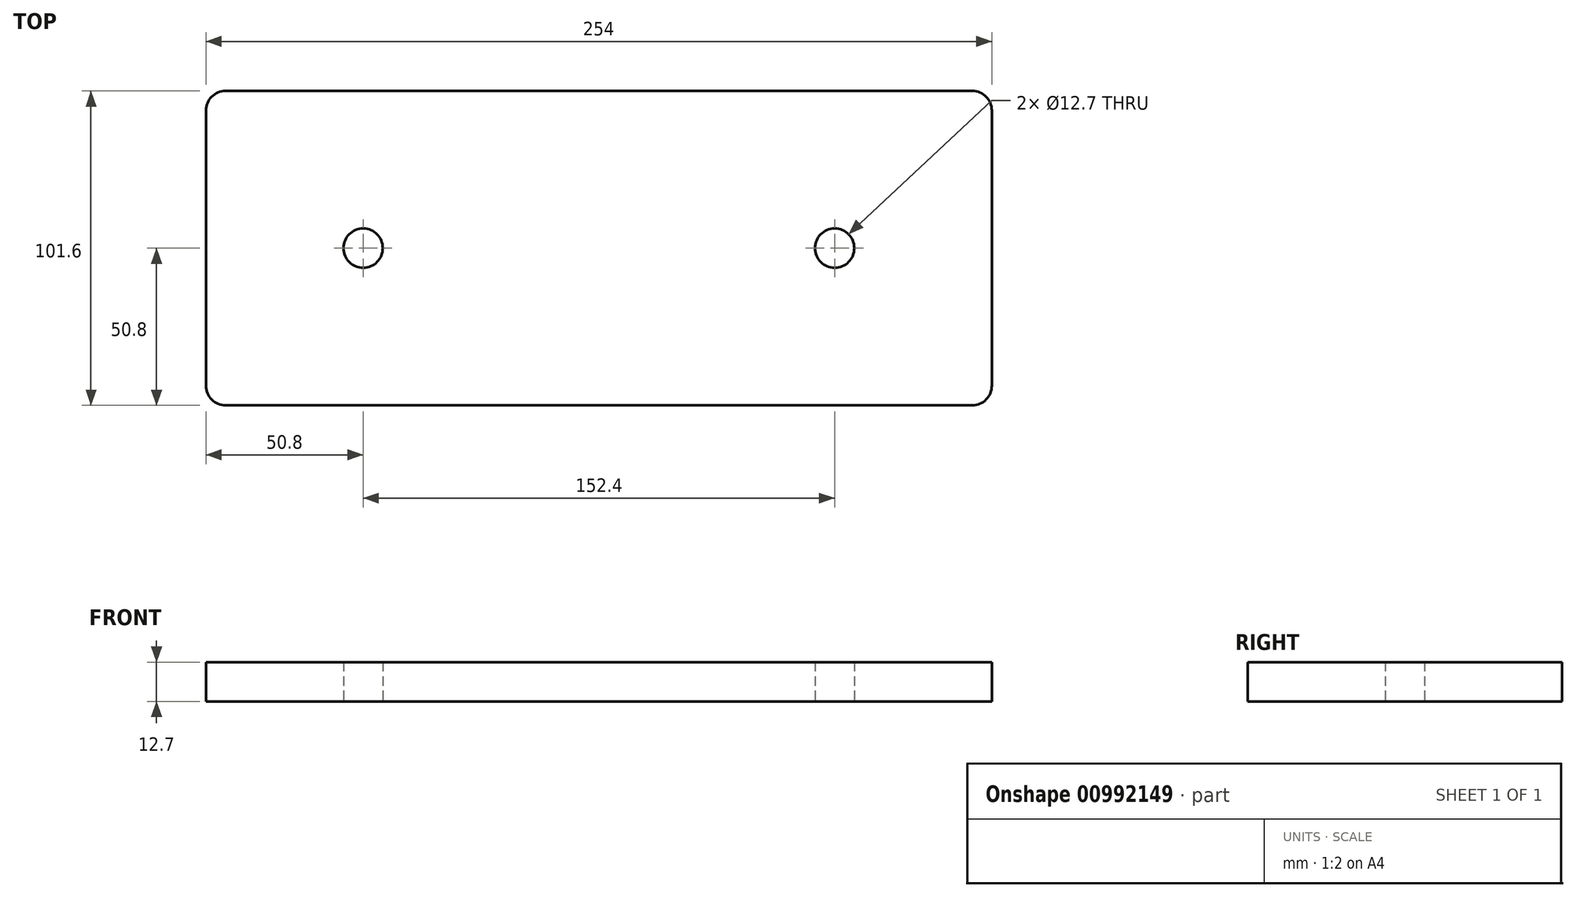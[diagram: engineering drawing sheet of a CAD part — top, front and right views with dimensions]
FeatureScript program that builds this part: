
annotation { "Feature Type Name" : "Feature", "Feature Type Description" : "" }
export const myFeature = defineFeature(function(context is Context, id is Id, definition is map)
    precondition{}
    {
        {
            var Q0;
            Q0=qCreatedBy(makeId("Top.planeOp"),FACE);
            var sketch = newSketch(context, id + "F0", { "sketchPlane" : qUnion([Q0])});
            skLineSegment(sketch, "E0.bottom", {"start": v(127, -50.8) * mm, "end": v(-127, -50.8) * mm});
            skLineSegment(sketch, "E0.top", {"start": v(127, 50.8) * mm, "end": v(-127, 50.8) * mm});
            skLineSegment(sketch, "E0.left", {"start": v(127, -50.8) * mm, "end": v(127, 50.8) * mm});
            skLineSegment(sketch, "E0.right", {"start": v(-127, -50.8) * mm, "end": v(-127, 50.8) * mm});
            skPoint(sketch, "E0.middle", {"position": v(0, 0) * mm});
            skPoint(sketch, "E1", {"position": v(-76.2, 0) * mm});
            skPoint(sketch, "E2", {"position": v(76.2, 0) * mm});
            skCircle(sketch, "E3", {"center": v(-76.2, 0) * mm, "radius": 6.35 * mm});
            skCircle(sketch, "E4", {"center": v(76.2, 0) * mm, "radius": 6.35 * mm});
            skPoint(sketch, "E5.orphan", {"position": v(-127, 0) * mm});
            skPoint(sketch, "E6.orphan", {"position": v(127, 0) * mm});
            skSolve(sketch);
        }
        {
            var Q0;
            Q0=makeQuery(id+"F0.imprint","IMPRINT",FACE,{"disambiguationData":[TD([[makeQuery(id+"F0.imprint","IMPRINT",EDGE,{"derivedFrom":sQuery(id+"F0.wireOp",EDGE,"E0.bottom")}),-1.0]])]});
            extrude(context, id + "F1", {"entities" : qUnion([Q0]), "depth" : 12.7 * mm, "offsetDistance" : 25.4 * mm});
        }
        {
            var Q0;
            Q0=makeQuery(id+"F1.opExtrude","SWEPT_EDGE",EDGE,{"disambiguationData":[OSD([sQuery(id+"F0.wireOp",EDGE,"E0.top"),sQuery(id+"F0.wireOp",EDGE,"E0.right")])]});
            var Q1;
            Q1=makeQuery(id+"F1.opExtrude","SWEPT_EDGE",EDGE,{"disambiguationData":[OSD([sQuery(id+"F0.wireOp",EDGE,"E0.bottom"),sQuery(id+"F0.wireOp",EDGE,"E0.right")])]});
            var Q2;
            Q2=makeQuery(id+"F1.opExtrude","SWEPT_EDGE",EDGE,{"disambiguationData":[OSD([sQuery(id+"F0.wireOp",EDGE,"E0.bottom"),sQuery(id+"F0.wireOp",EDGE,"E0.left")])]});
            var Q3;
            Q3=makeQuery(id+"F1.opExtrude","SWEPT_EDGE",EDGE,{"disambiguationData":[OSD([sQuery(id+"F0.wireOp",EDGE,"E0.top"),sQuery(id+"F0.wireOp",EDGE,"E0.left")])]});
            fillet(context, id + "F2", {"entities" : qUnion([Q0, Q1, Q2, Q3]), "radius" : 6.35 * mm, "tangentPropagation" : true, "allowEdgeOverflow" : false});
        }
    });
